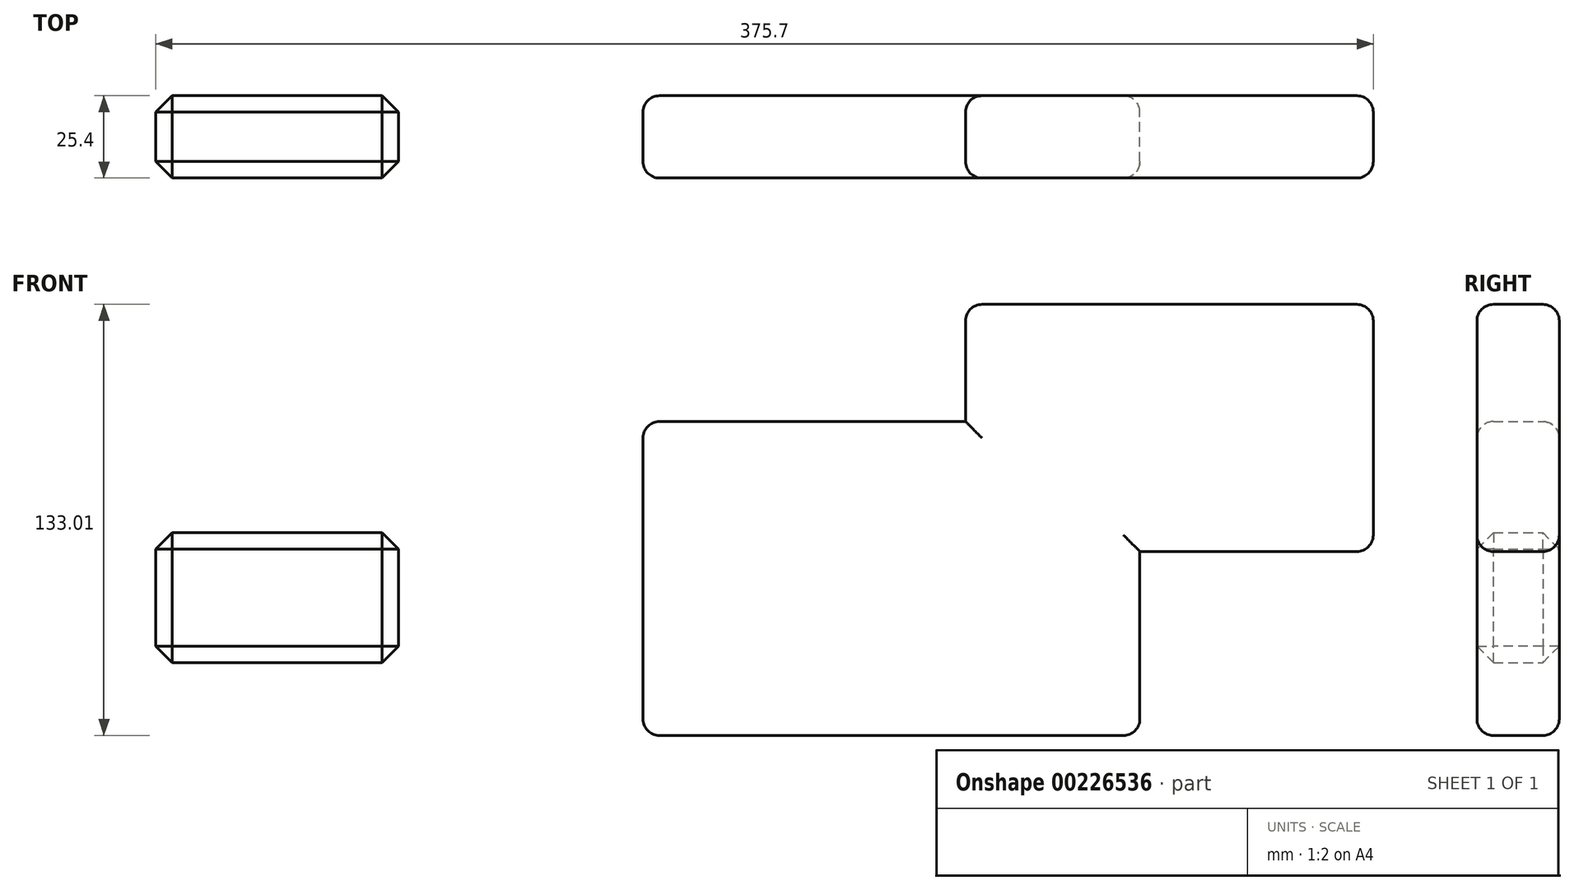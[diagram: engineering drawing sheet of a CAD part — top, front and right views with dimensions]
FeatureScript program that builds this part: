
annotation { "Feature Type Name" : "Feature", "Feature Type Description" : "" }
export const myFeature = defineFeature(function(context is Context, id is Id, definition is map)
    precondition{}
    {
        {
            var Q0;
            Q0=qCreatedBy(makeId("Front.planeOp"),FACE);
            var sketch = newSketch(context, id + "F0", { "sketchPlane" : qUnion([Q0])});
            skLineSegment(sketch, "E0.bottom", {"start": v(-126, 0) * mm, "end": v(-51.1, 0) * mm});
            skLineSegment(sketch, "E0.top", {"start": v(-126, -40.06) * mm, "end": v(-51.1, -40.06) * mm});
            skLineSegment(sketch, "E0.left", {"start": v(-126, 0) * mm, "end": v(-126, -40.06) * mm});
            skLineSegment(sketch, "E0.right", {"start": v(-51.1, 0) * mm, "end": v(-51.1, -40.06) * mm});
            skLineSegment(sketch, "E1.bottom", {"start": v(-186.3, -82.8) * mm, "end": v(-269.58, -82.8) * mm});
            skLineSegment(sketch, "E1.top", {"start": v(-186.3, -137.68) * mm, "end": v(-269.58, -137.68) * mm});
            skLineSegment(sketch, "E1.left", {"start": v(-186.3, -82.8) * mm, "end": v(-186.3, -137.68) * mm});
            skLineSegment(sketch, "E1.right", {"start": v(-269.58, -82.8) * mm, "end": v(-269.58, -137.68) * mm});
            skLineSegment(sketch, "E2.bottom", {"start": v(249.7, 70.47) * mm, "end": v(123.86, 70.47) * mm});
            skLineSegment(sketch, "E2.top", {"start": v(249.7, -5.78) * mm, "end": v(123.86, -5.78) * mm});
            skLineSegment(sketch, "E2.left", {"start": v(249.7, 70.47) * mm, "end": v(249.7, -5.78) * mm});
            skLineSegment(sketch, "E2.right", {"start": v(123.86, 70.47) * mm, "end": v(123.86, -5.78) * mm});
            skLineSegment(sketch, "E3.bottom", {"start": v(177.67, 34.32) * mm, "end": v(24.34, 34.32) * mm});
            skLineSegment(sketch, "E3.top", {"start": v(177.67, -62.54) * mm, "end": v(24.34, -62.54) * mm});
            skLineSegment(sketch, "E3.left", {"start": v(177.67, 34.32) * mm, "end": v(177.67, -62.54) * mm});
            skLineSegment(sketch, "E3.right", {"start": v(24.34, 34.32) * mm, "end": v(24.34, -62.54) * mm});
            skSolve(sketch);
        }
        {
            var Q0;
            Q0 = qSketchRegion(id + "F0", true);
            extrude(context, id + "F1", {"entities" : qUnion([Q0]), "depth" : 25.4 * mm});
        }
        {
            var Q0;
            Q0=makeQuery(id+"F1.opExtrude","CAP_EDGE",EDGE,{"disambiguationData":[OSD([sQuery(id+"F0.wireOp",EDGE,"E2.left")])],"isStart":true});
            fillet(context, id + "F2", {"entities" : qUnion([Q0]), "radius" : 5.08 * mm, "tangentPropagation" : true, "allowEdgeOverflow" : false});
        }
        {
            var Q0;
            Q0=makeQuery(id+"F1.opExtrude","CAP_EDGE",EDGE,{"disambiguationData":[OSD([sQuery(id+"F0.wireOp",EDGE,"E2.top")])],"isStart":true});
            fillet(context, id + "F3", {"entities" : qUnion([Q0]), "radius" : 5.08 * mm, "tangentPropagation" : true, "allowEdgeOverflow" : false});
        }
        {
            var Q0;
            Q0=makeQuery(id+"F1.opExtrude","CAP_EDGE",EDGE,{"disambiguationData":[OSD([sQuery(id+"F0.wireOp",EDGE,"E3.left")])],"isStart":true});
            fillet(context, id + "F4", {"entities" : qUnion([Q0]), "radius" : 5.08 * mm, "tangentPropagation" : true, "allowEdgeOverflow" : false});
        }
        {
            var Q0;
            Q0=makeQuery(id+"F1.opExtrude","CAP_EDGE",EDGE,{"disambiguationData":[OSD([sQuery(id+"F0.wireOp",EDGE,"E3.top")])],"isStart":true});
            fillet(context, id + "F5", {"entities" : qUnion([Q0]), "radius" : 5.08 * mm, "tangentPropagation" : true, "allowEdgeOverflow" : false});
        }
        {
            var Q0;
            Q0=makeQuery(id+"F1.opExtrude","CAP_EDGE",EDGE,{"disambiguationData":[OSD([sQuery(id+"F0.wireOp",EDGE,"E3.right")])],"isStart":true});
            fillet(context, id + "F6", {"entities" : qUnion([Q0]), "radius" : 5.08 * mm, "tangentPropagation" : true, "allowEdgeOverflow" : false});
        }
        {
            var Q0;
            Q0=makeQuery(id+"F1.opExtrude","CAP_EDGE",EDGE,{"disambiguationData":[OSD([sQuery(id+"F0.wireOp",EDGE,"E3.bottom")])],"isStart":true});
            fillet(context, id + "F7", {"entities" : qUnion([Q0]), "radius" : 5.08 * mm, "tangentPropagation" : true, "allowEdgeOverflow" : false});
        }
        {
            var Q0;
            Q0=makeQuery(id+"F1.opExtrude","CAP_EDGE",EDGE,{"disambiguationData":[OSD([sQuery(id+"F0.wireOp",EDGE,"E2.bottom")])],"isStart":true});
            fillet(context, id + "F8", {"entities" : qUnion([Q0]), "radius" : 5.08 * mm, "tangentPropagation" : true, "allowEdgeOverflow" : false});
        }
        {
            var Q0;
            Q0=makeQuery(id+"F1.opExtrude","CAP_EDGE",EDGE,{"disambiguationData":[OSD([sQuery(id+"F0.wireOp",EDGE,"E2.right")])],"isStart":true});
            fillet(context, id + "F9", {"entities" : qUnion([Q0]), "radius" : 5.08 * mm, "tangentPropagation" : true, "allowEdgeOverflow" : false});
        }
        {
            var Q0;
            Q0=makeQuery(id+"F1.opExtrude","CAP_FACE",FACE,{"disambiguationData":[OSD([sQuery(id+"F0.wireOp",EDGE,"E2.bottom"),sQuery(id+"F0.wireOp",EDGE,"E2.top"),sQuery(id+"F0.wireOp",EDGE,"E2.left"),sQuery(id+"F0.wireOp",EDGE,"E2.right"),sQuery(id+"F0.wireOp",EDGE,"E3.bottom"),sQuery(id+"F0.wireOp",EDGE,"E3.top"),sQuery(id+"F0.wireOp",EDGE,"E3.left"),sQuery(id+"F0.wireOp",EDGE,"E3.right")])],"isStart":false});
            fillet(context, id + "F10", {"entities" : qUnion([Q0]), "radius" : 5.08 * mm, "tangentPropagation" : true, "allowEdgeOverflow" : false});
        }
        {
            var Q0;
            Q0=makeQuery(id+"F1.opExtrude","SWEPT_BODY",BODY,{"disambiguationData":[OSD([sQuery(id+"F0.wireOp",EDGE,"E1.bottom"),sQuery(id+"F0.wireOp",EDGE,"E1.top"),sQuery(id+"F0.wireOp",EDGE,"E1.left"),sQuery(id+"F0.wireOp",EDGE,"E1.right")])]});
            deleteBodies(context, id + "F11", {"entities" : qUnion([Q0])});
        }
        {
            var Q0;
            Q0=makeQuery(id+"F1.opExtrude","SWEPT_FACE",FACE,{"disambiguationData":[OSD([sQuery(id+"F0.wireOp",EDGE,"E0.bottom")])]});
            var Q1;
            Q1=makeQuery(id+"F1.opExtrude","SWEPT_FACE",FACE,{"disambiguationData":[OSD([sQuery(id+"F0.wireOp",EDGE,"E0.right")])]});
            var Q2;
            Q2=makeQuery(id+"F1.opExtrude","CAP_FACE",FACE,{"disambiguationData":[OSD([sQuery(id+"F0.wireOp",EDGE,"E0.bottom"),sQuery(id+"F0.wireOp",EDGE,"E0.top"),sQuery(id+"F0.wireOp",EDGE,"E0.left"),sQuery(id+"F0.wireOp",EDGE,"E0.right")])],"isStart":true});
            var Q3;
            Q3=makeQuery(id+"F1.opExtrude","SWEPT_FACE",FACE,{"disambiguationData":[OSD([sQuery(id+"F0.wireOp",EDGE,"E0.top")])]});
            var Q4;
            Q4=makeQuery(id+"F1.opExtrude","SWEPT_FACE",FACE,{"disambiguationData":[OSD([sQuery(id+"F0.wireOp",EDGE,"E0.left")])]});
            chamfer(context, id + "F12", {"entities" : qUnion([Q0, Q1, Q2, Q3, Q4]), "width" : 5.08 * mm, "tangentPropagation" : true});
        }
    });
